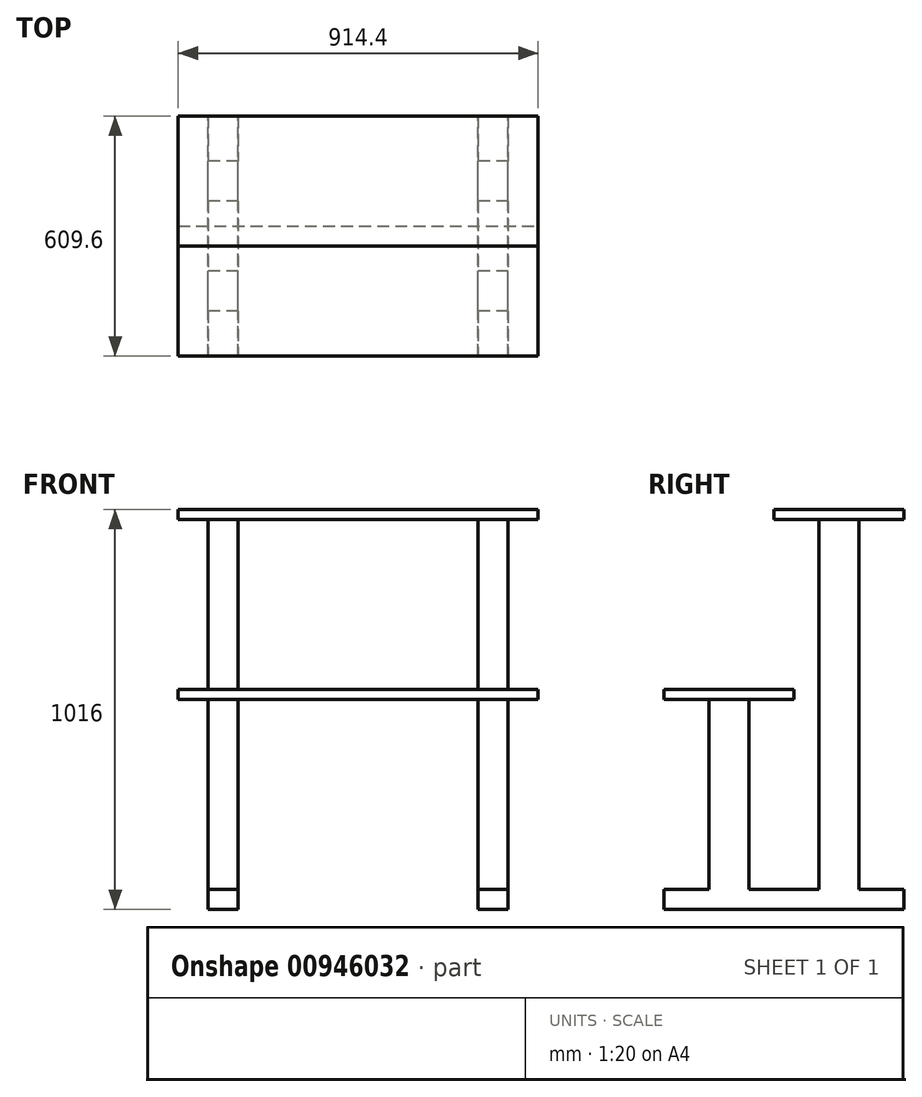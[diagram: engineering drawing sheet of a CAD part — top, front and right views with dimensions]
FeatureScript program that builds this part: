
annotation { "Feature Type Name" : "Feature", "Feature Type Description" : "" }
export const myFeature = defineFeature(function(context is Context, id is Id, definition is map)
    precondition{}
    {
        {
            var Q0;
            Q0=qCreatedBy(makeId("Top.planeOp"),FACE);
            var sketch = newSketch(context, id + "F0", { "sketchPlane" : qUnion([Q0])});
            skLineSegment(sketch, "E0.bottom", {"start": v(-457.2, 304.8) * mm, "end": v(457.2, 304.8) * mm});
            skLineSegment(sketch, "E0.top", {"start": v(-457.2, -304.8) * mm, "end": v(457.2, -304.8) * mm});
            skLineSegment(sketch, "E0.left", {"start": v(-457.2, 304.8) * mm, "end": v(-457.2, -304.8) * mm});
            skLineSegment(sketch, "E0.right", {"start": v(457.2, 304.8) * mm, "end": v(457.2, -304.8) * mm});
            skPoint(sketch, "E0.middle", {"position": v(0, 0) * mm});
            skSolve(sketch);
        }
        {
            var Q0;
            Q0=makeQuery(id+"F0.imprint","IMPRINT",FACE,{"disambiguationData":[TD([[makeQuery(id+"F0.imprint","IMPRINT",EDGE,{"derivedFrom":sQuery(id+"F0.wireOp",EDGE,"E0.bottom")}),-1.0]])]});
            extrude(context, id + "F1", {"entities" : qUnion([Q0]), "depth" : 1016 * mm, "offsetDistance" : 25.4 * mm});
        }
        {
            var Q0;
            Q0=makeQuery(id+"F1.opExtrude","CAP_FACE",FACE,{"disambiguationData":[OSD([sQuery(id+"F0.wireOp",EDGE,"E0.bottom"),sQuery(id+"F0.wireOp",EDGE,"E0.top"),sQuery(id+"F0.wireOp",EDGE,"E0.left"),sQuery(id+"F0.wireOp",EDGE,"E0.right")])],"isStart":false});
            var sketch = newSketch(context, id + "F2", { "sketchPlane" : qUnion([Q0])});
            skLineSegment(sketch, "E1.bottom", {"start": v(-457.2, 304.8) * mm, "end": v(457.2, 304.8) * mm});
            skLineSegment(sketch, "E1.top", {"start": v(-457.2, -25.4) * mm, "end": v(457.2, -25.4) * mm});
            skLineSegment(sketch, "E1.left", {"start": v(-457.2, 304.8) * mm, "end": v(-457.2, -25.4) * mm});
            skLineSegment(sketch, "E1.right", {"start": v(457.2, 304.8) * mm, "end": v(457.2, -25.4) * mm});
            skSolve(sketch);
        }
        {
            var Q0;
            {var subQ0=sQuery(id+"F2.wireOp",EDGE,"E1.top");Q0=makeQuery(id+"F2.imprint","IMPRINT",FACE,{"disambiguationData":[TD([[makeQuery(id+"F2.imprint","IMPRINT",EDGE,{"derivedFrom":subQ0}),-1.0]])]});}
            extrude(context, id + "F3", {"entities" : qUnion([Q0]), "operationType" : NewBodyOperationType.REMOVE, "oppositeDirection" : true, "depth" : 457.2 * mm, "offsetDistance" : 25.4 * mm});
        }
        {
            var Q0;
            Q0=makeQuery(id+"F1.opExtrude","CAP_FACE",FACE,{"disambiguationData":[OSD([sQuery(id+"F0.wireOp",EDGE,"E0.bottom"),sQuery(id+"F0.wireOp",EDGE,"E0.top"),sQuery(id+"F0.wireOp",EDGE,"E0.left"),sQuery(id+"F0.wireOp",EDGE,"E0.right")])],"isStart":true});
            var sketch = newSketch(context, id + "F4", { "sketchPlane" : qUnion([Q0])});
            skLineSegment(sketch, "E2.bottom", {"start": v(-457.2, 304.8) * mm, "end": v(-381, 304.8) * mm});
            skLineSegment(sketch, "E2.top", {"start": v(-457.2, -304.8) * mm, "end": v(-381, -304.8) * mm});
            skLineSegment(sketch, "E2.left", {"start": v(-457.2, 304.8) * mm, "end": v(-457.2, -304.8) * mm});
            skLineSegment(sketch, "E2.right", {"start": v(-381, 304.8) * mm, "end": v(-381, -304.8) * mm});
            skLineSegment(sketch, "E3.bottom", {"start": v(457.2, 304.8) * mm, "end": v(381, 304.8) * mm});
            skLineSegment(sketch, "E3.top", {"start": v(457.2, -304.8) * mm, "end": v(381, -304.8) * mm});
            skLineSegment(sketch, "E3.left", {"start": v(457.2, 304.8) * mm, "end": v(457.2, -304.8) * mm});
            skLineSegment(sketch, "E3.right", {"start": v(381, 304.8) * mm, "end": v(381, -304.8) * mm});
            skLineSegment(sketch, "E4.bottom", {"start": v(-381, 304.8) * mm, "end": v(-304.8, 304.8) * mm});
            skLineSegment(sketch, "E4.top", {"start": v(-381, -304.8) * mm, "end": v(-304.8, -304.8) * mm});
            skLineSegment(sketch, "E4.right", {"start": v(-304.8, 304.8) * mm, "end": v(-304.8, -304.8) * mm});
            skLineSegment(sketch, "E5.bottom", {"start": v(381, 304.8) * mm, "end": v(304.8, 304.8) * mm});
            skLineSegment(sketch, "E5.top", {"start": v(381, -304.8) * mm, "end": v(304.8, -304.8) * mm});
            skLineSegment(sketch, "E5.right", {"start": v(304.8, 304.8) * mm, "end": v(304.8, -304.8) * mm});
            skSolve(sketch);
        }
        {
            var Q0;
            Q0=makeQuery(id+"F4.imprint","IMPRINT",FACE,{"disambiguationData":[TD([[makeQuery(id+"F4.imprint","IMPRINT",EDGE,{"derivedFrom":sQuery(id+"F4.wireOp",EDGE,"E2.bottom")}),-1.0]])]});
            var Q1;
            Q1=makeQuery(id+"F4.imprint","IMPRINT",FACE,{"disambiguationData":[TD([[makeQuery(id+"F4.imprint","IMPRINT",EDGE,{"derivedFrom":sQuery(id+"F4.wireOp",EDGE,"E3.bottom")}),-1.0]])]});
            var Q2;
            {var subQ0=sQuery(id+"F4.wireOp",EDGE,"E4.right");Q2=makeQuery(id+"F4.imprint","IMPRINT",FACE,{"disambiguationData":[TD([[makeQuery(id+"F4.imprint","IMPRINT",EDGE,{"derivedFrom":subQ0}),1.0]])]});}
            extrude(context, id + "F5", {"entities" : qUnion([Q0, Q1, Q2]), "operationType" : NewBodyOperationType.REMOVE, "oppositeDirection" : true, "depth" : 533.4 * mm, "offsetDistance" : 25.4 * mm});
        }
        {
            var Q0;
            Q0=makeQuery(id+"F1.opExtrude","SWEPT_FACE",FACE,{"disambiguationData":[OSD([sQuery(id+"F0.wireOp",EDGE,"E0.left")])]});
            var sketch = newSketch(context, id + "F6", { "sketchPlane" : qUnion([Q0])});
            skLineSegment(sketch, "E6.bottom", {"start": v(-304.8, 1016) * mm, "end": v(25.4, 1016) * mm});
            skLineSegment(sketch, "E6.top", {"start": v(-304.8, 990.6) * mm, "end": v(25.4, 990.6) * mm});
            skLineSegment(sketch, "E6.left", {"start": v(-304.8, 1016) * mm, "end": v(-304.8, 990.6) * mm});
            skLineSegment(sketch, "E6.right", {"start": v(25.4, 1016) * mm, "end": v(25.4, 990.6) * mm});
            skLineSegment(sketch, "E7.bottom", {"start": v(25.4, 990.6) * mm, "end": v(0, 990.6) * mm});
            skLineSegment(sketch, "E7.top", {"start": v(25.4, 558.8) * mm, "end": v(0, 558.8) * mm});
            skLineSegment(sketch, "E7.left", {"start": v(25.4, 990.6) * mm, "end": v(25.4, 558.8) * mm});
            skLineSegment(sketch, "E7.right", {"start": v(0, 990.6) * mm, "end": v(0, 558.8) * mm});
            skSolve(sketch);
        }
        {
            var Q0;
            Q0=makeQuery(id+"F6.imprint","IMPRINT",FACE,{"disambiguationData":[TD([[makeQuery(id+"F6.imprint","IMPRINT",EDGE,{"derivedFrom":sQuery(id+"F6.wireOp",EDGE,"E7.top")}),-1.0]])]});
            extrude(context, id + "F7", {"entities" : qUnion([Q0]), "operationType" : NewBodyOperationType.REMOVE, "oppositeDirection" : true, "depth" : 914.4 * mm, "offsetDistance" : 25.4 * mm});
        }
        {
            var Q0;
            Q0=makeQuery(id+"F1.opExtrude","SWEPT_FACE",FACE,{"disambiguationData":[OSD([sQuery(id+"F0.wireOp",EDGE,"E0.bottom")])]});
            var sketch = newSketch(context, id + "F8", { "sketchPlane" : qUnion([Q0])});
            skLineSegment(sketch, "E8.bottom", {"start": v(-457.2, 1016) * mm, "end": v(457.2, 1016) * mm});
            skLineSegment(sketch, "E8.top", {"start": v(-457.2, 990.6) * mm, "end": v(457.2, 990.6) * mm});
            skLineSegment(sketch, "E8.left", {"start": v(-457.2, 1016) * mm, "end": v(-457.2, 990.6) * mm});
            skLineSegment(sketch, "E8.right", {"start": v(457.2, 1016) * mm, "end": v(457.2, 990.6) * mm});
            skLineSegment(sketch, "E9.bottom", {"start": v(-457.2, 1016) * mm, "end": v(-381, 1016) * mm});
            skLineSegment(sketch, "E9.top", {"start": v(-457.2, 533.4) * mm, "end": v(-381, 533.4) * mm});
            skLineSegment(sketch, "E9.left", {"start": v(-457.2, 1016) * mm, "end": v(-457.2, 533.4) * mm});
            skLineSegment(sketch, "E9.right", {"start": v(-381, 1016) * mm, "end": v(-381, 533.4) * mm});
            skLineSegment(sketch, "E10.bottom", {"start": v(457.2, 1016) * mm, "end": v(381, 1016) * mm});
            skLineSegment(sketch, "E10.top", {"start": v(457.2, 533.4) * mm, "end": v(381, 533.4) * mm});
            skLineSegment(sketch, "E10.left", {"start": v(457.2, 1016) * mm, "end": v(457.2, 533.4) * mm});
            skLineSegment(sketch, "E10.right", {"start": v(381, 1016) * mm, "end": v(381, 533.4) * mm});
            skLineSegment(sketch, "E11.bottom", {"start": v(-381, 1016) * mm, "end": v(-304.8, 1016) * mm});
            skLineSegment(sketch, "E11.top", {"start": v(-381, 533.4) * mm, "end": v(-304.8, 533.4) * mm});
            skLineSegment(sketch, "E11.right", {"start": v(-304.8, 1016) * mm, "end": v(-304.8, 533.4) * mm});
            skLineSegment(sketch, "E12.bottom", {"start": v(381, 1016) * mm, "end": v(304.8, 1016) * mm});
            skLineSegment(sketch, "E12.top", {"start": v(381, 533.4) * mm, "end": v(304.8, 533.4) * mm});
            skLineSegment(sketch, "E12.right", {"start": v(304.8, 1016) * mm, "end": v(304.8, 533.4) * mm});
            skLineSegment(sketch, "E13.bottom", {"start": v(-457.2, 533.4) * mm, "end": v(457.2, 533.4) * mm});
            skLineSegment(sketch, "E13.top", {"start": v(-457.2, 558.8) * mm, "end": v(457.2, 558.8) * mm});
            skLineSegment(sketch, "E13.left", {"start": v(-457.2, 533.4) * mm, "end": v(-457.2, 558.8) * mm});
            skLineSegment(sketch, "E13.right", {"start": v(457.2, 533.4) * mm, "end": v(457.2, 558.8) * mm});
            skSolve(sketch);
        }
        {
            var Q0;
            {var subQ0=sQuery(id+"F8.wireOp",EDGE,"E9.top");Q0=makeQuery(id+"F8.imprint","IMPRINT",FACE,{"disambiguationData":[TD([[makeQuery(id+"F8.imprint","IMPRINT",EDGE,{"derivedFrom":subQ0}),-1.0]])]});}
            var Q1;
            {var subQ0=sQuery(id+"F8.wireOp",EDGE,"E13.bottom");Q1=makeQuery(id+"F8.imprint","IMPRINT",FACE,{"disambiguationData":[TD([[makeQuery(id+"F8.imprint","IMPRINT",EDGE,{"derivedFrom":subQ0}),-1.0]])]});}
            var Q2;
            {var subQ0=sQuery(id+"F8.wireOp",EDGE,"E10.top");Q2=makeQuery(id+"F8.imprint","IMPRINT",FACE,{"disambiguationData":[TD([[makeQuery(id+"F8.imprint","IMPRINT",EDGE,{"derivedFrom":subQ0}),-1.0]])]});}
            extrude(context, id + "F9", {"entities" : qUnion([Q0, Q1, Q2]), "operationType" : NewBodyOperationType.REMOVE, "oppositeDirection" : true, "depth" : 279.4 * mm, "offsetDistance" : 25.4 * mm});
        }
        {
            var Q0;
            {var subQ0=sQuery(id+"F8.wireOp",EDGE,"E11.right");var subQ1=sQuery(id+"F8.wireOp",EDGE,"E8.top");var subQ2=makeQuery(id+"F8.imprint","INTERSECT",VERTEX,{"derivedFrom":[subQ1,subQ0]});Q0=makeQuery(id+"F8.imprint","IMPRINT",FACE,{"disambiguationData":[TD([[makeQuery(id+"F8.imprint","IMPRINT",EDGE,{"disambiguationData":[TD([[subQ2,-1.0]])],"derivedFrom":subQ1}),-1.0]])]});}
            extrude(context, id + "F10", {"entities" : qUnion([Q0]), "operationType" : NewBodyOperationType.REMOVE, "oppositeDirection" : true, "depth" : 431.8 * mm, "offsetDistance" : 25.4 * mm});
        }
        {
            var Q0;
            {var subQ0=sQuery(id+"F8.wireOp",EDGE,"E9.right");var subQ1=sQuery(id+"F8.wireOp",EDGE,"E8.top");var subQ2=makeQuery(id+"F8.imprint","INTERSECT",VERTEX,{"derivedFrom":[subQ1,subQ0]});Q0=makeQuery(id+"F8.imprint","IMPRINT",FACE,{"disambiguationData":[TD([[makeQuery(id+"F8.imprint","IMPRINT",EDGE,{"disambiguationData":[TD([[subQ2,-1.0]])],"derivedFrom":subQ0}),-1.0]])]});}
            var Q1;
            {var subQ1=sQuery(id+"F8.wireOp",EDGE,"E8.top");var subQ3=sQuery(id+"F8.wireOp",EDGE,"E10.right");var subQ4=makeQuery(id+"F8.imprint","INTERSECT",VERTEX,{"derivedFrom":[subQ1,subQ3]});Q1=makeQuery(id+"F8.imprint","IMPRINT",FACE,{"disambiguationData":[TD([[makeQuery(id+"F8.imprint","IMPRINT",EDGE,{"disambiguationData":[TD([[subQ4,-1.0]])],"derivedFrom":subQ3}),1.0]])]});}
            extrude(context, id + "F11", {"entities" : qUnion([Q0, Q1]), "operationType" : NewBodyOperationType.REMOVE, "oppositeDirection" : true, "depth" : 330.2 * mm, "offsetDistance" : 25.4 * mm});
        }
        {
            var Q0;
            {var subQ0=sQuery(id+"F8.wireOp",EDGE,"E10.right");Q0=makeQuery(id+"F11.boolean.opBoolean","MERGE",FACE,{"derivedFrom":[makeQuery(id+"F9.boolean.opBoolean","MERGE",FACE,{"derivedFrom":[makeQuery(id+"F5.boolean.opBoolean","COPY",FACE,{"derivedFrom":makeQuery(id+"F5.opExtrude","SWEPT_FACE",FACE,{"disambiguationData":[OSD([sQuery(id+"F4.wireOp",EDGE,"E2.right")])]})})],"fromTools":[makeQuery(id+"F9.opExtrude","SWEPT_FACE",FACE,{"disambiguationData":[OSD([subQ0])]})]})],"fromTools":[makeQuery(id+"F11.opExtrude","SWEPT_FACE",FACE,{"disambiguationData":[OSD([subQ0])]})]});}
            var sketch = newSketch(context, id + "F12", { "sketchPlane" : qUnion([Q0])});
            skLineSegment(sketch, "E14.bottom", {"start": v(-304.8, 990.6) * mm, "end": v(-190.5, 990.6) * mm});
            skLineSegment(sketch, "E14.top", {"start": v(-304.8, 0) * mm, "end": v(-190.5, 0) * mm});
            skLineSegment(sketch, "E14.left", {"start": v(-304.8, 990.6) * mm, "end": v(-304.8, 0) * mm});
            skLineSegment(sketch, "E14.right", {"start": v(-190.5, 990.6) * mm, "end": v(-190.5, 0) * mm});
            skLineSegment(sketch, "E15.bottom", {"start": v(-190.5, 990.6) * mm, "end": v(-88.9, 990.6) * mm});
            skLineSegment(sketch, "E15.top", {"start": v(-190.5, 0) * mm, "end": v(-88.9, 0) * mm});
            skLineSegment(sketch, "E15.right", {"start": v(-88.9, 990.6) * mm, "end": v(-88.9, 0) * mm});
            skLineSegment(sketch, "E16.bottom", {"start": v(-304.8, 0) * mm, "end": v(304.8, 0) * mm});
            skLineSegment(sketch, "E16.top", {"start": v(-304.8, 50.8) * mm, "end": v(304.8, 50.8) * mm});
            skLineSegment(sketch, "E16.left", {"start": v(-304.8, 0) * mm, "end": v(-304.8, 50.8) * mm});
            skLineSegment(sketch, "E16.right", {"start": v(304.8, 0) * mm, "end": v(304.8, 50.8) * mm});
            skLineSegment(sketch, "E17.bottom", {"start": v(-88.9, 990.6) * mm, "end": v(0, 990.6) * mm});
            skLineSegment(sketch, "E17.top", {"start": v(-88.9, 558.8) * mm, "end": v(0, 558.8) * mm});
            skLineSegment(sketch, "E17.left", {"start": v(-88.9, 990.6) * mm, "end": v(-88.9, 558.8) * mm});
            skLineSegment(sketch, "E17.right", {"start": v(0, 990.6) * mm, "end": v(0, 558.8) * mm});
            skLineSegment(sketch, "E18.bottom", {"start": v(-88.9, 558.8) * mm, "end": v(-25.4, 558.8) * mm});
            skLineSegment(sketch, "E18.top", {"start": v(-88.9, 50.8) * mm, "end": v(-25.4, 50.8) * mm});
            skLineSegment(sketch, "E18.left", {"start": v(-88.9, 558.8) * mm, "end": v(-88.9, 50.8) * mm});
            skLineSegment(sketch, "E18.right", {"start": v(-25.4, 558.8) * mm, "end": v(-25.4, 50.8) * mm});
            skLineSegment(sketch, "E19.bottom", {"start": v(304.8, 533.4) * mm, "end": v(190.5, 533.4) * mm});
            skLineSegment(sketch, "E19.top", {"start": v(304.8, 50.8) * mm, "end": v(190.5, 50.8) * mm});
            skLineSegment(sketch, "E19.left", {"start": v(304.8, 533.4) * mm, "end": v(304.8, 50.8) * mm});
            skLineSegment(sketch, "E19.right", {"start": v(190.5, 533.4) * mm, "end": v(190.5, 50.8) * mm});
            skLineSegment(sketch, "E20.bottom", {"start": v(190.5, 533.4) * mm, "end": v(88.9, 533.4) * mm});
            skLineSegment(sketch, "E20.top", {"start": v(190.5, 50.8) * mm, "end": v(88.9, 50.8) * mm});
            skLineSegment(sketch, "E20.right", {"start": v(88.9, 533.4) * mm, "end": v(88.9, 50.8) * mm});
            skSolve(sketch);
        }
        {
            var Q0;
            {var subQ0=sQuery(id+"F12.wireOp",EDGE,"E14.bottom");Q0=makeQuery(id+"F12.imprint","IMPRINT",FACE,{"disambiguationData":[TD([[makeQuery(id+"F12.imprint","IMPRINT",EDGE,{"derivedFrom":subQ0}),1.0]])]});}
            extrude(context, id + "F13", {"entities" : qUnion([Q0]), "operationType" : NewBodyOperationType.REMOVE, "oppositeDirection" : true, "depth" : 777.24 * mm, "offsetDistance" : 25.4 * mm});
        }
        {
            var Q0;
            {var subQ5=sQuery(id+"F12.wireOp",EDGE,"E17.bottom");Q0=makeQuery(id+"F12.imprint","IMPRINT",FACE,{"disambiguationData":[TD([[makeQuery(id+"F12.imprint","IMPRINT",EDGE,{"derivedFrom":subQ5}),1.0]])]});}
            var Q1;
            {var subQ1=sQuery(id+"F12.wireOp",EDGE,"E17.top");var subQ3=sQuery(id+"F12.wireOp",EDGE,"E15.right");var subQ4=makeQuery(id+"F12.imprint","INTERSECT",VERTEX,{"derivedFrom":[subQ3,subQ1]});Q1=makeQuery(id+"F12.imprint","IMPRINT",FACE,{"disambiguationData":[TD([[makeQuery(id+"F12.imprint","IMPRINT",EDGE,{"disambiguationData":[TD([[subQ4,-1.0]])],"derivedFrom":subQ3}),1.0]])]});}
            var Q2;
            {var subQ3=sQuery(id+"F12.wireOp",EDGE,"E20.right");Q2=makeQuery(id+"F12.imprint","IMPRINT",FACE,{"disambiguationData":[TD([[makeQuery(id+"F12.imprint","IMPRINT",EDGE,{"derivedFrom":subQ3}),-1.0]])]});}
            var Q3;
            Q3=makeQuery(id+"F12.imprint","IMPRINT",FACE,{"disambiguationData":[TD([[makeQuery(id+"F12.imprint","IMPRINT",EDGE,{"derivedFrom":sQuery(id+"F12.wireOp",EDGE,"E19.bottom")}),1.0]])]});
            extrude(context, id + "F14", {"entities" : qUnion([Q0, Q1, Q2, Q3]), "operationType" : NewBodyOperationType.REMOVE, "oppositeDirection" : true, "depth" : 878.84 * mm, "offsetDistance" : 25.4 * mm});
        }
    });
